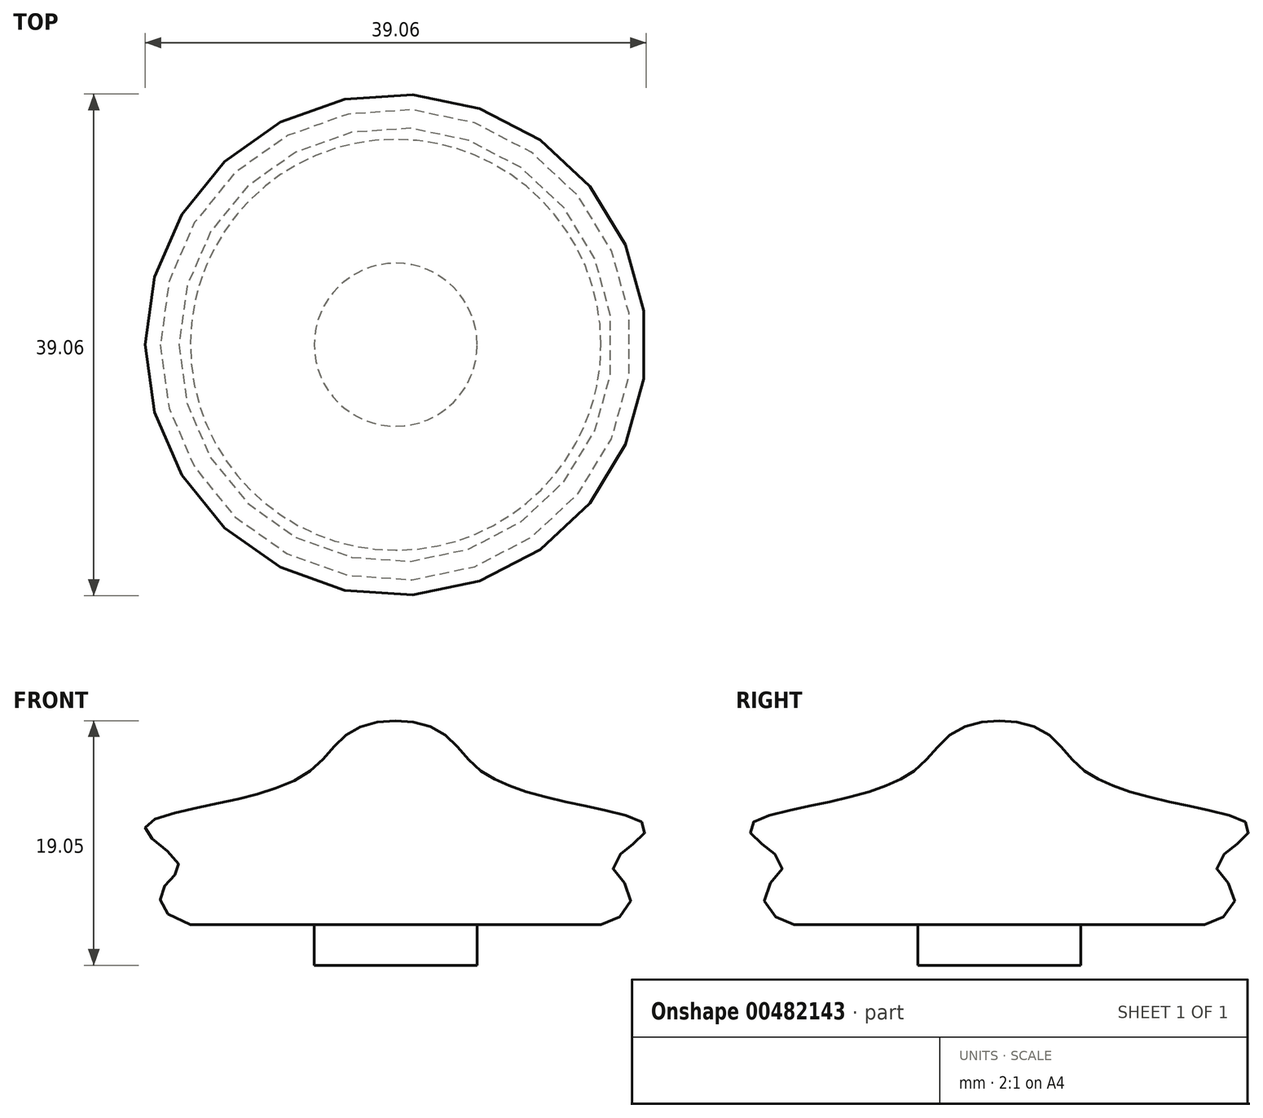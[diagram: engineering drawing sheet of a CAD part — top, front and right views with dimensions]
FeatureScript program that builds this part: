
annotation { "Feature Type Name" : "Feature", "Feature Type Description" : "" }
export const myFeature = defineFeature(function(context is Context, id is Id, definition is map)
    precondition{}
    {
        {
            var Q0;
            Q0=qCreatedBy(makeId("Front.planeOp"),FACE);
            var sketch = newSketch(context, id + "F0", { "sketchPlane" : qUnion([Q0])});
            skLineSegment(sketch, "E0", {"start": v(0, 0) * mm, "end": v(-6.35, 0) * mm});
            skLineSegment(sketch, "E1", {"start": v(-6.35, 0) * mm, "end": v(-6.35, 3.17) * mm});
            skLineSegment(sketch, "E2", {"start": v(-6.35, 3.17) * mm, "end": v(-16, 3.17) * mm});
            skFitSpline(sketch, "E3", {"points": [v(-16, 3.17) * mm, v(-18.17, 5.92) * mm, v(-16.92, 7.87) * mm, v(-19.52, 10.56) * mm, v(-16, 12.15) * mm, v(-10.67, 13.37) * mm, v(-6.35, 15.37) * mm, v(-3.76, 18.02) * mm, v(0, 19.05) * mm], "startDerivative": vector(-54.7, 13.36) * mm, "endDerivative": vector(34.35, 0.24) * mm});
            skLineSegment(sketch, "E4", {"start": v(0, 0) * mm, "end": v(0, 19.05) * mm});
            skSolve(sketch);
        }
        {
            var Q0;
            Q0=makeQuery(id+"F0.imprint","IMPRINT",FACE,{"disambiguationData":[TD([[makeQuery(id+"F0.imprint","IMPRINT",EDGE,{"derivedFrom":sQuery(id+"F0.wireOp",EDGE,"E0")}),-1.0]])]});
            var Q1;
            Q1=sQuery(id+"F0.wireOp",EDGE,"E4");
            revolve(context, id + "F1", {"entities" : qUnion([Q0]), "axis" : qUnion([Q1]), "revolveType" : RevolveType.FULL});
        }
    });
